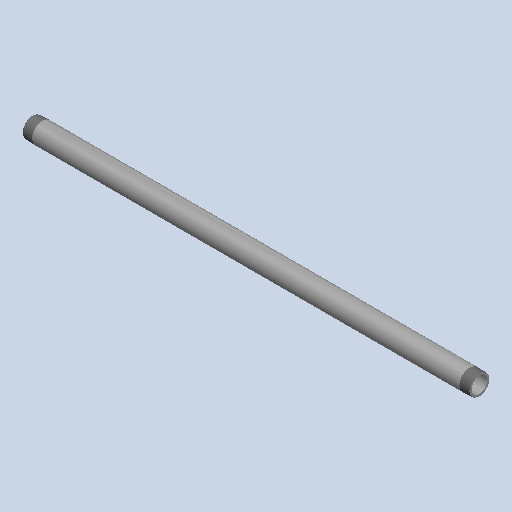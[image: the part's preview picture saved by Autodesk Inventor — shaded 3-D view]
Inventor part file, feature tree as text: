
AUTODESK INVENTOR PART (.ipt)
format: ipt  version: 2025 (Build 290162000, 162)  size: 172,032 bytes
history: native  units: mm (DEFAULTED — no unit token found)
features: other x8, revolve x1
ambient origin geometry x8: Origin, YZ Plane, XZ Plane, XY Plane, X Axis, Y Axis, Z Axis, Center Point
bodies: Solid1 (feature_tree)
feature tree (9):
  revolve  "Revolution1"  [1 undecoded]
  other  "Work Axis1"
  other  "Work Point5"
  other  "Work Axis2"
  other  "Work Point6"
  other  "Work Axis3"
  other  "Work Axis4"
  other  "Work Point7"
  other  "Work Point8"
note: 1 required parameter value undecoded (feature->parameter linkage not recoverable at this tier; creation-order binding heuristic only, values carry confidence <= 0.55)
